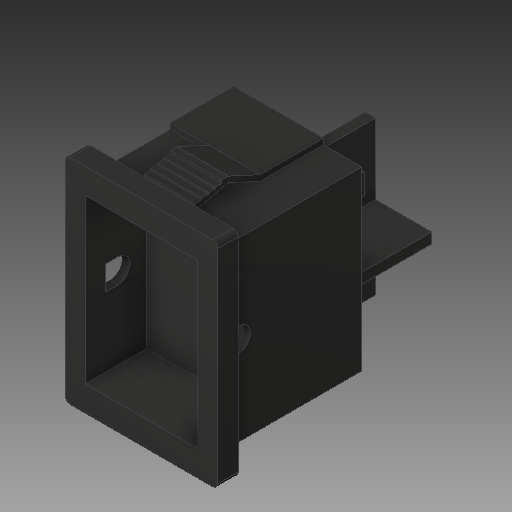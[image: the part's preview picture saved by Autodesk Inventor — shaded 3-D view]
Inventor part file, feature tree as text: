
AUTODESK INVENTOR PART (.ipt)
format: ipt  version: 2019.4 (Build 234330000, 330)  size: 169,472 bytes
history: native  units: mm
features: fillet x1
ambient origin geometry x8: Origin, YZ Plane, XZ Plane, XY Plane, X Axis, Y Axis, Z Axis, Center Point
bodies: Solid1 (feature_tree)
feature tree (1):
  fillet  "Fillet1"  [1 undecoded]
note: 1 required parameter value undecoded (feature->parameter linkage not recoverable at this tier; creation-order binding heuristic only, values carry confidence <= 0.55)
